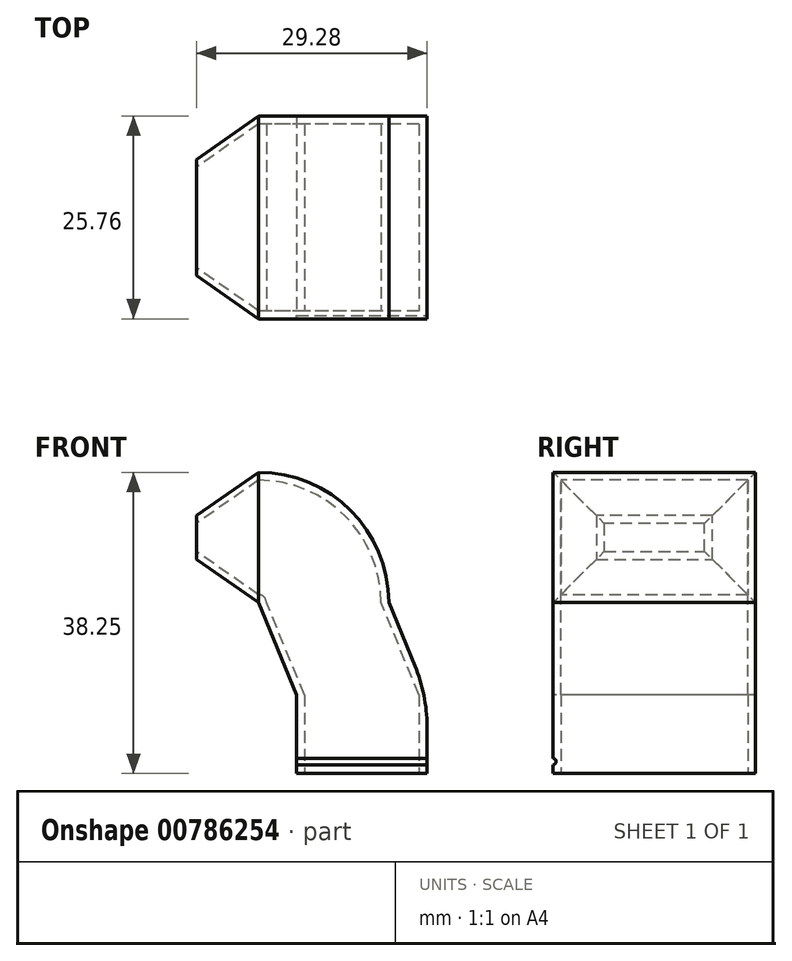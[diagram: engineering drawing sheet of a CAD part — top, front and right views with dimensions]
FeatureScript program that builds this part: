
annotation { "Feature Type Name" : "Feature", "Feature Type Description" : "" }
export const myFeature = defineFeature(function(context is Context, id is Id, definition is map)
    precondition{}
    {
        {
            var Q0;
            Q0=qCreatedBy(makeId("Top.planeOp"),FACE);
            var sketch = newSketch(context, id + "F0", { "sketchPlane" : qUnion([Q0])});
            skLineSegment(sketch, "E0.bottom", {"start": v(8.28, 12.88) * mm, "end": v(-8.27, 12.88) * mm});
            skLineSegment(sketch, "E0.top", {"start": v(8.28, -12.88) * mm, "end": v(-8.28, -12.88) * mm});
            skLineSegment(sketch, "E0.left", {"start": v(8.28, 12.88) * mm, "end": v(8.28, -12.88) * mm});
            skLineSegment(sketch, "E0.right", {"start": v(-8.27, 12.88) * mm, "end": v(-8.28, -12.88) * mm});
            skPoint(sketch, "E0.middle", {"position": v(0, 0) * mm});
            skLineSegment(sketch, "E1.0", {"start": v(-7.27, 11.88) * mm, "end": v(-7.28, -11.88) * mm});
            skLineSegment(sketch, "E1.1", {"start": v(7.28, 11.88) * mm, "end": v(-7.27, 11.88) * mm});
            skLineSegment(sketch, "E1.2", {"start": v(7.28, 11.88) * mm, "end": v(7.28, -11.88) * mm});
            skLineSegment(sketch, "E1.3", {"start": v(7.28, -11.88) * mm, "end": v(-7.28, -11.88) * mm});
            skSolve(sketch);
        }
        {
            var Q0;
            Q0 = qSketchRegion(id + "F0", true);
            extrude(context, id + "F1", {"entities" : qUnion([Q0]), "depth" : 10 * mm, "offsetDistance" : 25 * mm});
        }
        {
            var Q0;
            Q0=makeQuery(id+"F1.opExtrude","SWEPT_FACE",FACE,{"disambiguationData":[OSD([sQuery(id+"F0.wireOp",EDGE,"E0.left")])]});
            var sketch = newSketch(context, id + "F2", { "sketchPlane" : qUnion([Q0])});
            skCircle(sketch, "E2", {"center": v(-12.88, 1.5) * mm, "radius": 0.4 * mm});
            skSolve(sketch);
        }
        {
            var Q0;
            {var subQ0=sQuery(id+"F2.wireOp",EDGE,"E2");var subQ1=makeQuery(id+"F1.opExtrude","SWEPT_EDGE",EDGE,{"disambiguationData":[OSD([sQuery(id+"F0.wireOp",EDGE,"E0.top"),sQuery(id+"F0.wireOp",EDGE,"E0.left")])]});var subQ2=makeQuery(id+"F2.imprint","INTERSECT",VERTEX,{"disambiguationData":[OD(0.0)],"derivedFrom":[subQ1,subQ0]});Q0=makeQuery(id+"F2.imprint","IMPRINT",FACE,{"disambiguationData":[TD([[makeQuery(id+"F2.imprint","IMPRINT",EDGE,{"disambiguationData":[TD([[subQ2,-1.0]])],"derivedFrom":subQ0}),1.0]])]});}
            extrude(context, id + "F3", {"entities" : qUnion([Q0]), "operationType" : NewBodyOperationType.REMOVE, "oppositeDirection" : true, "depth" : 25 * mm, "offsetDistance" : 25 * mm});
        }
        {
            var Q0;
            Q0=makeQuery(id+"F1.opExtrude","CAP_EDGE",EDGE,{"disambiguationData":[OSD([sQuery(id+"F0.wireOp",EDGE,"E0.right")])],"isStart":false});
            cPlane(context, id + "F4", {"entities" : qUnion([Q0]), "cplaneType" : CPlaneType.LINE_ANGLE, "offset" : 25 * mm, "angle" : 45 * degree, "width" : 150 * mm, "height" : 150 * mm});
        }
        {
            var Q0;
            Q0=qCreatedBy(id+"F4.planeOp",FACE);
            var sketch = newSketch(context, id + "F5", { "sketchPlane" : qUnion([Q0])});
            skLineSegment(sketch, "E3.0", {"start": v(1.22, -12.88) * mm, "end": v(1.22, 12.88) * mm});
            skLineSegment(sketch, "E4.bottom", {"start": v(1.22, 12.88) * mm, "end": v(17.77, 12.88) * mm});
            skLineSegment(sketch, "E4.top", {"start": v(1.22, -12.88) * mm, "end": v(17.77, -12.88) * mm});
            skLineSegment(sketch, "E4.left", {"start": v(1.22, 12.88) * mm, "end": v(1.22, -12.88) * mm});
            skLineSegment(sketch, "E4.right", {"start": v(17.77, 12.88) * mm, "end": v(17.77, -12.88) * mm});
            skLineSegment(sketch, "E5.0", {"start": v(16.77, 11.88) * mm, "end": v(16.77, -11.88) * mm});
            skLineSegment(sketch, "E5.1", {"start": v(2.22, 11.88) * mm, "end": v(16.77, 11.88) * mm});
            skLineSegment(sketch, "E5.2", {"start": v(2.22, 11.88) * mm, "end": v(2.22, -11.88) * mm});
            skLineSegment(sketch, "E5.3", {"start": v(2.22, -11.88) * mm, "end": v(16.77, -11.88) * mm});
            skSolve(sketch);
        }
        {
            var Q0;
            Q0=qCreatedBy(makeId("Front.planeOp"),FACE);
            var sketch = newSketch(context, id + "F6", { "sketchPlane" : qUnion([Q0])});
            skLineSegment(sketch, "E6", {"start": v(3.43, 21.7) * mm, "end": v(8.28, 10) * mm});
            skSolve(sketch);
        }
        {
            var Q0;
            Q0=makeQuery(id+"F1.opExtrude","CAP_FACE",FACE,{"disambiguationData":[OSD([sQuery(id+"F0.wireOp",EDGE,"E0.bottom"),sQuery(id+"F0.wireOp",EDGE,"E0.top"),sQuery(id+"F0.wireOp",EDGE,"E0.left"),sQuery(id+"F0.wireOp",EDGE,"E0.right"),sQuery(id+"F0.wireOp",EDGE,"E1.0"),sQuery(id+"F0.wireOp",EDGE,"E1.1"),sQuery(id+"F0.wireOp",EDGE,"E1.2"),sQuery(id+"F0.wireOp",EDGE,"E1.3")])],"isStart":false});
            var Q1;
            Q1 = qConstructionFilter(qBodyType(qCreatedBy(id + "F6" ,EDGE), BodyType.WIRE), ConstructionObject.NO);
            sweep(context, id + "F7", {"operationType" : NewBodyOperationType.ADD, "profiles" : qUnion([Q0]), "path" : qUnion([Q1]), "keepProfileOrientation" : true});
        }
        {
            var Q0;
            {var subQ0=sQuery(id+"F0.wireOp",EDGE,"E0.left");Q0=makeQuery(id+"F7.boolean.opBoolean","MERGE",EDGE,{"derivedFrom":[makeQuery(id+"F1.opExtrude","CAP_EDGE",EDGE,{"disambiguationData":[OSD([subQ0])],"isStart":false}),makeQuery(id+"F7.opSweep","CAP_EDGE",EDGE,{"disambiguationData":[OSD([subQ0,sQuery(id+"F6.wireOp",VERTEX,"E6.end")])],"isStart":true})]});}
            fillet(context, id + "F8", {"entities" : qUnion([Q0]), "radius" : 20 * mm, "tangentPropagation" : true, "allowEdgeOverflow" : false});
        }
        {
            var Q0;
            Q0=qCreatedBy(makeId("Right.planeOp"),FACE);
            var Q1;
            Q1=makeQuery(id+"F7.opSweep","CAP_VERTEX",VERTEX,{"disambiguationData":[OSD([sQuery(id+"F0.wireOp",EDGE,"E0.bottom"),sQuery(id+"F0.wireOp",EDGE,"E0.right"),sQuery(id+"F6.wireOp",EDGE,"E6")])],"isStart":false});
            cPlane(context, id + "F9", {"entities" : qUnion([Q0, Q1]), "cplaneType" : CPlaneType.PLANE_POINT, "offset" : 13 * mm, "oppositeDirection" : true, "width" : 150 * mm, "height" : 150 * mm});
        }
        {
            var Q0;
            Q0=qCreatedBy(id+"F9.planeOp",FACE);
            var sketch = newSketch(context, id + "F10", { "sketchPlane" : qUnion([Q0])});
            skLineSegment(sketch, "E7.0", {"start": v(12.88, 21.7) * mm, "end": v(-12.88, 21.7) * mm});
            skLineSegment(sketch, "E8.top", {"start": v(12.88, 38.25) * mm, "end": v(-12.88, 38.25) * mm});
            skLineSegment(sketch, "E8.left", {"start": v(12.87, 21.7) * mm, "end": v(12.88, 38.25) * mm});
            skLineSegment(sketch, "E8.right", {"start": v(-12.88, 21.7) * mm, "end": v(-12.88, 38.25) * mm});
            skSolve(sketch);
        }
        {
            var Q0;
            Q0=qCreatedBy(makeId("Front.planeOp"),FACE);
            var sketch = newSketch(context, id + "F11", { "sketchPlane" : qUnion([Q0])});
            skLineSegment(sketch, "E9", {"start": v(3.43, 21.7) * mm, "end": v(3.43, 21.7) * mm});
            skLineSegment(sketch, "E10", {"start": v(-13.12, 38.25) * mm, "end": v(-13.12, 38.25) * mm});
            skPoint(sketch, "E11.visualSharp", {"position": v(3.43, 38.25) * mm});
            skArc(sketch, "E11.filletArc", {"start": v(3.43, 21.7) * mm, "mid": v(-1.42, 33.4) * mm, "end": v(-13.12, 38.25) * mm});
            skSolve(sketch);
        }
        {
            var Q0;
            Q0=makeQuery(id+"F7.opSweep","CAP_FACE",FACE,{"disambiguationData":[OSD([sQuery(id+"F0.wireOp",EDGE,"E0.bottom"),sQuery(id+"F0.wireOp",EDGE,"E0.top"),sQuery(id+"F0.wireOp",EDGE,"E0.left"),sQuery(id+"F0.wireOp",EDGE,"E0.right"),sQuery(id+"F0.wireOp",EDGE,"E1.0"),sQuery(id+"F0.wireOp",EDGE,"E1.1"),sQuery(id+"F0.wireOp",EDGE,"E1.2"),sQuery(id+"F0.wireOp",EDGE,"E1.3"),sQuery(id+"F6.wireOp",VERTEX,"E6.start")])],"isStart":false});
            var Q1;
            Q1=sQuery(id+"F11.wireOp",EDGE,"E11.filletArc");
            sweep(context, id + "F12", {"operationType" : NewBodyOperationType.ADD, "profiles" : qUnion([Q0]), "path" : qUnion([Q1])});
        }
        {
            var Q0;
            Q0=qCreatedBy(makeId("Right.planeOp"),FACE);
            cPlane(context, id + "F13", {"entities" : qUnion([Q0]), "cplaneType" : CPlaneType.OFFSET, "offset" : 21 * mm, "oppositeDirection" : true, "width" : 150 * mm, "height" : 150 * mm});
        }
        {
            var Q0;
            Q0=qCreatedBy(id+"F13.planeOp",FACE);
            var sketch = newSketch(context, id + "F14", { "sketchPlane" : qUnion([Q0])});
            skLineSegment(sketch, "E12.0", {"start": v(7.38, 32.75) * mm, "end": v(-7.38, 32.75) * mm});
            skLineSegment(sketch, "E12.1", {"start": v(7.38, 27.2) * mm, "end": v(7.38, 32.75) * mm});
            skLineSegment(sketch, "E12.2", {"start": v(-7.38, 27.2) * mm, "end": v(7.38, 27.2) * mm});
            skLineSegment(sketch, "E12.3", {"start": v(-7.38, 32.75) * mm, "end": v(-7.38, 27.2) * mm});
            skLineSegment(sketch, "E13.0", {"start": v(6.38, 31.75) * mm, "end": v(-6.38, 31.75) * mm});
            skLineSegment(sketch, "E13.1", {"start": v(6.38, 28.2) * mm, "end": v(6.38, 31.75) * mm});
            skLineSegment(sketch, "E13.2", {"start": v(-6.38, 28.2) * mm, "end": v(6.38, 28.2) * mm});
            skLineSegment(sketch, "E13.3", {"start": v(-6.38, 31.75) * mm, "end": v(-6.38, 28.2) * mm});
            skSolve(sketch);
        }
        {
            var Q0;
            Q0=qCreatedBy(makeId("Front.planeOp"),FACE);
            var sketch = newSketch(context, id + "F15", { "sketchPlane" : qUnion([Q0])});
            skLineSegment(sketch, "E14.0", {"start": v(-13.12, 21.7) * mm, "end": v(-13.12, 38.25) * mm});
            skLineSegment(sketch, "E15.0", {"start": v(-21, 27.2) * mm, "end": v(-21, 32.75) * mm});
            skLineSegment(sketch, "E16", {"start": v(-21, 32.75) * mm, "end": v(-13.12, 38.25) * mm});
            skLineSegment(sketch, "E17", {"start": v(-21, 27.2) * mm, "end": v(-13.12, 21.7) * mm});
            skLineSegment(sketch, "E18.0", {"start": v(-21, 28.2) * mm, "end": v(-21, 31.75) * mm});
            skLineSegment(sketch, "E19.0", {"start": v(-13.12, 22.7) * mm, "end": v(-13.12, 37.25) * mm});
            skLineSegment(sketch, "E20", {"start": v(-13.12, 37.25) * mm, "end": v(-21, 31.75) * mm});
            skSolve(sketch);
        }
        {
            var Q0;
            {var subQ0=sQuery(id+"F15.wireOp",EDGE,"E16");Q0=makeQuery(id+"F15.imprint","IMPRINT",FACE,{"disambiguationData":[TD([[makeQuery(id+"F15.imprint","IMPRINT",EDGE,{"derivedFrom":subQ0}),-1.0]])]});}
            var Q1;
            Q1=sQuery(id+"F14.wireOp",EDGE,"E12.3");
            var Q2;
            Q2=sQuery(id+"F14.wireOp",EDGE,"E12.0");
            var Q3;
            Q3=sQuery(id+"F14.wireOp",EDGE,"E12.1");
            var Q4;
            Q4=sQuery(id+"F14.wireOp",EDGE,"E12.2");
            sweep(context, id + "F16", {"operationType" : NewBodyOperationType.ADD, "profiles" : qUnion([Q0]), "path" : qUnion([Q1, Q2, Q3, Q4])});
        }
    });
